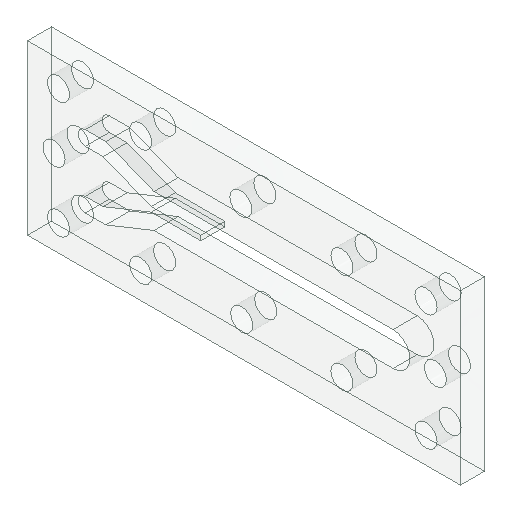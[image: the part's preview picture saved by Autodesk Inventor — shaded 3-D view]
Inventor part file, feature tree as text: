
AUTODESK INVENTOR PART (.ipt)
format: ipt  version: 2025 (Build 290162000, 162)  size: 146,944 bytes
history: native  units: mm
features: other x1, extrude x1, sketch x1
ambient origin geometry x8: Origin, YZ Plane, XZ Plane, XY Plane, X Axis, Y Axis, Z Axis, Center Point
bodies: Body1 (feature_tree)
feature tree (3):
  other  "Sólido1"
  extrude  "Extrusão1"  [1 undecoded]
  sketch  "Esboço1"  dims[d0=5.0mm d1=0.0mm]
note: 1 required parameter value undecoded (feature->parameter linkage not recoverable at this tier; creation-order binding heuristic only, values carry confidence <= 0.55)
